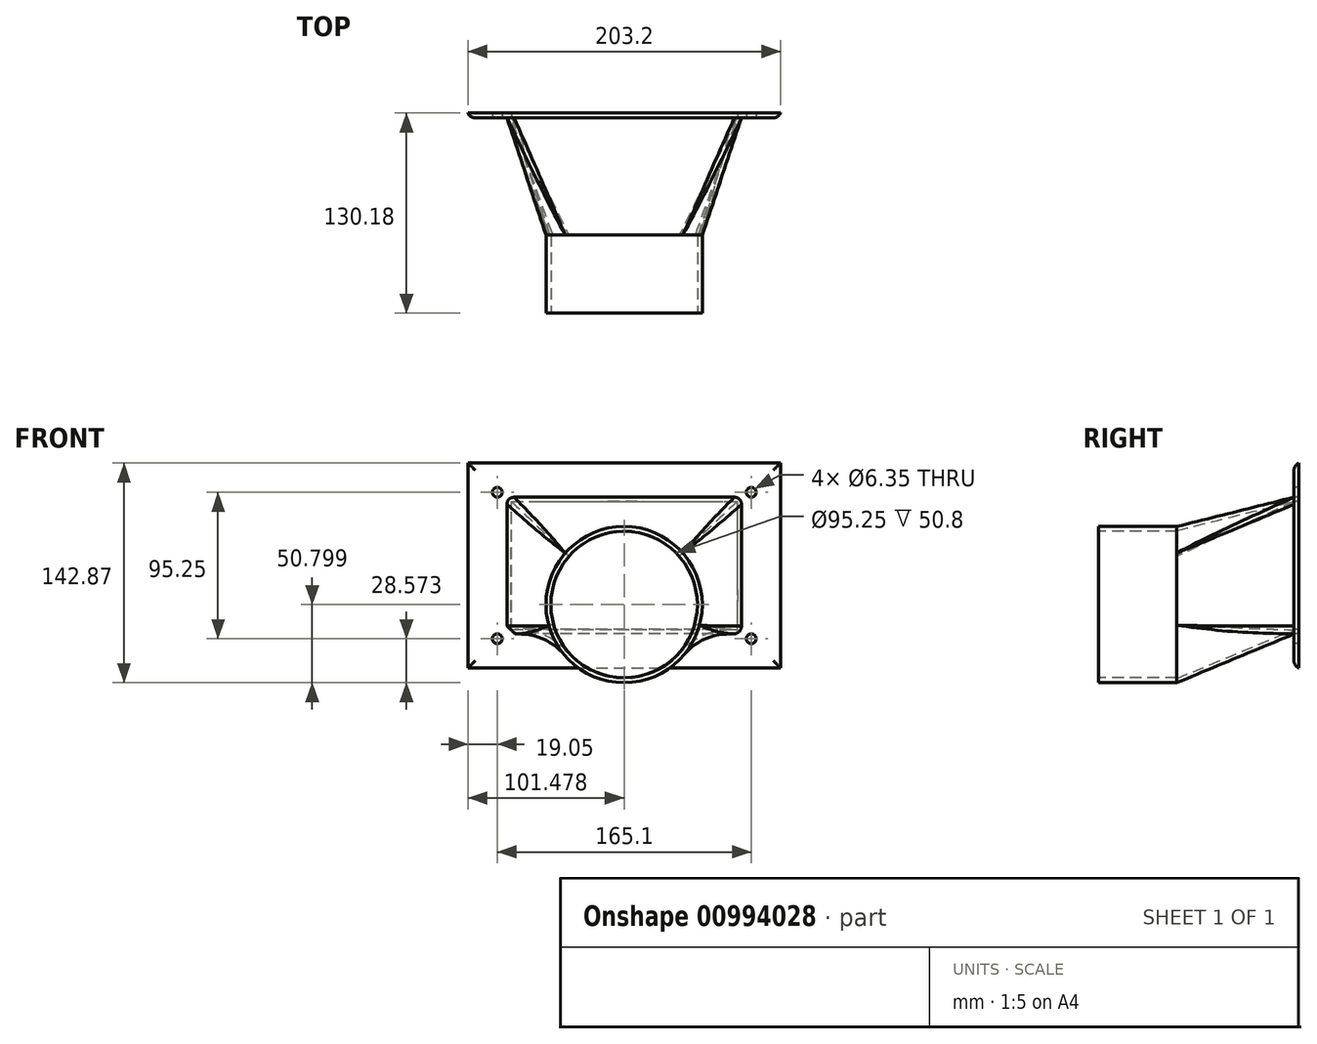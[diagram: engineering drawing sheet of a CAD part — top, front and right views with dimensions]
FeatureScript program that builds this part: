
annotation { "Feature Type Name" : "Feature", "Feature Type Description" : "" }
export const myFeature = defineFeature(function(context is Context, id is Id, definition is map)
    precondition{}
    {
        {
            var Q0;
            Q0=qCreatedBy(makeId("Front.planeOp"),FACE);
            var sketch = newSketch(context, id + "F0", { "sketchPlane" : qUnion([Q0])});
            skPoint(sketch, "E0.middle", {"position": v(0, 0.32) * mm});
            skPoint(sketch, "E1.startSnap0", {"position": v(-101.6, 0.32) * mm});
            skLineSegment(sketch, "E2.bottom", {"start": v(76.2, -44.13) * mm, "end": v(-76.2, -44.13) * mm});
            skLineSegment(sketch, "E2.top", {"start": v(76.2, 44.77) * mm, "end": v(-76.2, 44.77) * mm});
            skLineSegment(sketch, "E2.left", {"start": v(76.2, -44.13) * mm, "end": v(76.2, 44.77) * mm});
            skLineSegment(sketch, "E2.right", {"start": v(-76.2, -44.13) * mm, "end": v(-76.2, 44.77) * mm});
            skSolve(sketch);
        }
        {
            var Q0;
            Q0=qCreatedBy(makeId("Front.planeOp"),FACE);
            cPlane(context, id + "F1", {"entities" : qUnion([Q0]), "cplaneType" : CPlaneType.OFFSET, "offset" : 76.2 * mm, "width" : 152.4 * mm, "height" : 152.4 * mm});
        }
        {
            var Q0;
            Q0=qCreatedBy(id+"F1.planeOp",FACE);
            var sketch = newSketch(context, id + "F2", { "sketchPlane" : qUnion([Q0])});
            skArc(sketch, "E3", {"start": v(-38.37, 8.35) * mm, "mid": v(-49.67, -13.89) * mm, "end": v(-49.03, -38.83) * mm});
            skArc(sketch, "E4", {"start": v(38.06, 8.42) * mm, "mid": v(-0.17, 25.72) * mm, "end": v(-38.37, 8.35) * mm});
            skArc(sketch, "E5", {"start": v(48.86, -38.56) * mm, "mid": v(49.39, -13.7) * mm, "end": v(38.06, 8.42) * mm});
            skArc(sketch, "E6", {"start": v(-49.03, -38.83) * mm, "mid": v(0.02, -75.88) * mm, "end": v(48.86, -38.56) * mm});
            skSolve(sketch);
        }
        {
            var Q0;
            Q0=makeQuery(id+"F0.imprint","IMPRINT",FACE,{"disambiguationData":[TD([[makeQuery(id+"F0.imprint","IMPRINT",EDGE,{"derivedFrom":sQuery(id+"F0.wireOp",EDGE,"E2.bottom")}),-1.0]])]});
            var Q1;
            Q1=makeQuery(id+"F2.imprint","IMPRINT",FACE,{"disambiguationData":[TD([[makeQuery(id+"F2.imprint","IMPRINT",EDGE,{"derivedFrom":sQuery(id+"F2.wireOp",EDGE,"E3")}),1.0]])]});
            loft(context, id + "F3", {"sheetProfilesArray" : [{ "sheetProfileEntities" : qUnion([Q0]) }, { "sheetProfileEntities" : qUnion([Q1]) }]});
        }
        {
            var Q0;
            Q0 = qSketchRegion(id + "F0", true);
            extrude(context, id + "F4", {"entities" : qUnion([Q0]), "operationType" : NewBodyOperationType.ADD, "oppositeDirection" : true, "depth" : 3.17 * mm, "offsetDistance" : 25.4 * mm});
        }
        {
            var Q0;
            Q0 = qSketchRegion(id + "F2", true);
            extrude(context, id + "F5", {"entities" : qUnion([Q0]), "depth" : 50.8 * mm, "offsetDistance" : 25.4 * mm});
        }
        {
            var Q0;
            Q0=makeQuery(id+"F5.opExtrude","CAP_FACE",FACE,{"disambiguationData":[OSD([sQuery(id+"F2.wireOp",EDGE,"E3"),sQuery(id+"F2.wireOp",EDGE,"E4"),sQuery(id+"F2.wireOp",EDGE,"E5"),sQuery(id+"F2.wireOp",EDGE,"E6")])],"isStart":false});
            var sketch = newSketch(context, id + "F6", { "sketchPlane" : qUnion([Q0])});
            skCircle(sketch, "E7", {"center": v(-0.12, -25.08) * mm, "radius": 47.63 * mm});
            skSolve(sketch);
        }
        {
            var Q0;
            Q0 = qSketchRegion(id + "F6", true);
            extrude(context, id + "F7", {"entities" : qUnion([Q0]), "operationType" : NewBodyOperationType.REMOVE, "oppositeDirection" : true, "depth" : 50.8 * mm, "offsetDistance" : 25.4 * mm});
        }
        {
            var Q0;
            Q0=makeQuery(id+"F4.opExtrude","CAP_FACE",FACE,{"disambiguationData":[OSD([sQuery(id+"F0.wireOp",EDGE,"E2.bottom"),sQuery(id+"F0.wireOp",EDGE,"E2.top"),sQuery(id+"F0.wireOp",EDGE,"E2.left"),sQuery(id+"F0.wireOp",EDGE,"E2.right")])],"isStart":false});
            var Q1;
            Q1=makeQuery(id+"F3.opLoft","CAP_FACE",FACE,{"disambiguationData":[OSD([makeQuery(id+"F2.imprint","IMPRINT",FACE,{"disambiguationData":[TD([[makeQuery(id+"F2.imprint","IMPRINT",EDGE,{"derivedFrom":sQuery(id+"F2.wireOp",EDGE,"E3")}),1.0]])]})])],"isStart":true});
            shell(context, id + "F8", {"entities" : qUnion([Q0, Q1]), "thickness" : 2.54 * mm});
        }
        {
            var Q0;
            Q0=makeQuery(id+"F0.imprint","IMPRINT",FACE,{"disambiguationData":[TD([[makeQuery(id+"F0.imprint","IMPRINT",EDGE,{"derivedFrom":sQuery(id+"F0.wireOp",EDGE,"E2.bottom")}),-1.0]])]});
            var sketch = newSketch(context, id + "F9", { "sketchPlane" : qUnion([Q0])});
            skLineSegment(sketch, "E8.bottom", {"start": v(-82.55, -47.3) * mm, "end": v(82.55, -47.3) * mm, "construction": true});
            skLineSegment(sketch, "E8.top", {"start": v(-82.55, 47.94) * mm, "end": v(82.55, 47.94) * mm, "construction": true});
            skLineSegment(sketch, "E8.left", {"start": v(-82.55, -47.3) * mm, "end": v(-82.55, 47.94) * mm, "construction": true});
            skLineSegment(sketch, "E8.right", {"start": v(82.55, -47.3) * mm, "end": v(82.55, 47.94) * mm, "construction": true});
            skPoint(sketch, "E8.middle", {"position": v(0, 0.32) * mm});
            skCircle(sketch, "E9", {"center": v(82.55, 47.94) * mm, "radius": 3.17 * mm});
            skCircle(sketch, "E10", {"center": v(-82.55, 47.94) * mm, "radius": 3.18 * mm});
            skCircle(sketch, "E11", {"center": v(-82.55, -47.3) * mm, "radius": 3.18 * mm});
            skCircle(sketch, "E12", {"center": v(82.55, -47.3) * mm, "radius": 3.18 * mm});
            skLineSegment(sketch, "E13.bottom", {"start": v(-101.6, -66.36) * mm, "end": v(101.6, -66.36) * mm});
            skLineSegment(sketch, "E13.top", {"start": v(-101.6, 67) * mm, "end": v(101.6, 67) * mm});
            skLineSegment(sketch, "E13.left", {"start": v(-101.6, -66.36) * mm, "end": v(-101.6, 67) * mm});
            skLineSegment(sketch, "E13.right", {"start": v(101.6, -66.36) * mm, "end": v(101.6, 67) * mm});
            skSolve(sketch);
        }
        {
            var Q0;
            Q0 = qSketchRegion(id + "F9", true);
            extrude(context, id + "F10", {"entities" : qUnion([Q0]), "operationType" : NewBodyOperationType.ADD, "oppositeDirection" : true, "depth" : 3.17 * mm, "offsetDistance" : 25.4 * mm});
        }
        {
            var Q0;
            Q0=makeQuery(id+"F9.imprint","IMPRINT",FACE,{"disambiguationData":[TD([[makeQuery(id+"F9.imprint","IMPRINT",EDGE,{"derivedFrom":makeQuery(id+"F0.imprint","IMPRINT",EDGE,{"derivedFrom":sQuery(id+"F0.wireOp",EDGE,"E2.bottom")})}),-1.0]])]});
            var sketch = newSketch(context, id + "F11", { "sketchPlane" : qUnion([Q0])});
            skLineSegment(sketch, "E14.bottom", {"start": v(-73.35, -41.29) * mm, "end": v(73.54, -41.29) * mm});
            skLineSegment(sketch, "E14.top", {"start": v(-73.35, 42.05) * mm, "end": v(73.54, 42.05) * mm});
            skLineSegment(sketch, "E14.left", {"start": v(-73.35, -41.29) * mm, "end": v(-73.35, 42.05) * mm});
            skLineSegment(sketch, "E14.right", {"start": v(73.54, -41.29) * mm, "end": v(73.54, 42.05) * mm});
            skPoint(sketch, "E14.middle", {"position": v(0.1, 0.38) * mm});
            skSolve(sketch);
        }
        {
            var Q0;
            Q0 = qSketchRegion(id + "F11", true);
            extrude(context, id + "F12", {"entities" : qUnion([Q0]), "operationType" : NewBodyOperationType.REMOVE, "oppositeDirection" : true, "depth" : 3.17 * mm, "offsetDistance" : 25.4 * mm});
        }
        {
            var Q0;
            Q0=makeQuery(id+"F3.opLoft","SWEPT_EDGE",EDGE,{"disambiguationData":[OSD([sQuery(id+"F0.wireOp",EDGE,"E2.bottom"),sQuery(id+"F0.wireOp",EDGE,"E2.right"),sQuery(id+"F2.wireOp",EDGE,"E3"),sQuery(id+"F2.wireOp",EDGE,"E6")])]});
            chamfer(context, id + "F13", {"entities" : qUnion([Q0]), "width" : 5.08 * mm, "tangentPropagation" : true});
        }
        {
            var Q0;
            Q0=makeQuery(id+"F10.opExtrude","CAP_EDGE",EDGE,{"disambiguationData":[OSD([sQuery(id+"F9.wireOp",EDGE,"E13.top")])],"isStart":true});
            var Q1;
            Q1=makeQuery(id+"F10.opExtrude","CAP_EDGE",EDGE,{"disambiguationData":[OSD([sQuery(id+"F9.wireOp",EDGE,"E13.left")])],"isStart":true});
            var Q2;
            Q2=makeQuery(id+"F10.opExtrude","CAP_EDGE",EDGE,{"disambiguationData":[OSD([sQuery(id+"F9.wireOp",EDGE,"E13.right")])],"isStart":true});
            var Q3;
            Q3=makeQuery(id+"F10.opExtrude","CAP_EDGE",EDGE,{"disambiguationData":[OSD([sQuery(id+"F9.wireOp",EDGE,"E13.bottom")])],"isStart":true});
            var Q4;
            Q4=makeQuery(id+"F3.opLoft","SWEPT_EDGE",EDGE,{"disambiguationData":[OSD([sQuery(id+"F0.wireOp",EDGE,"E2.top"),sQuery(id+"F0.wireOp",EDGE,"E2.right"),sQuery(id+"F2.wireOp",EDGE,"E3"),sQuery(id+"F2.wireOp",EDGE,"E4")])]});
            var Q5;
            Q5=makeQuery(id+"F3.opLoft","SWEPT_EDGE",EDGE,{"disambiguationData":[OSD([sQuery(id+"F0.wireOp",EDGE,"E2.top"),sQuery(id+"F0.wireOp",EDGE,"E2.left"),sQuery(id+"F2.wireOp",EDGE,"E4"),sQuery(id+"F2.wireOp",EDGE,"E5")])]});
            var Q6;
            Q6=makeQuery(id+"F3.opLoft","SWEPT_EDGE",EDGE,{"disambiguationData":[OSD([sQuery(id+"F0.wireOp",EDGE,"E2.bottom"),sQuery(id+"F0.wireOp",EDGE,"E2.left"),sQuery(id+"F2.wireOp",EDGE,"E5"),sQuery(id+"F2.wireOp",EDGE,"E6")])]});
            fillet(context, id + "F14", {"entities" : qUnion([Q0, Q1, Q2, Q3, Q4, Q5, Q6]), "radius" : 5.08 * mm, "tangentPropagation" : true, "allowEdgeOverflow" : false});
        }
    });
